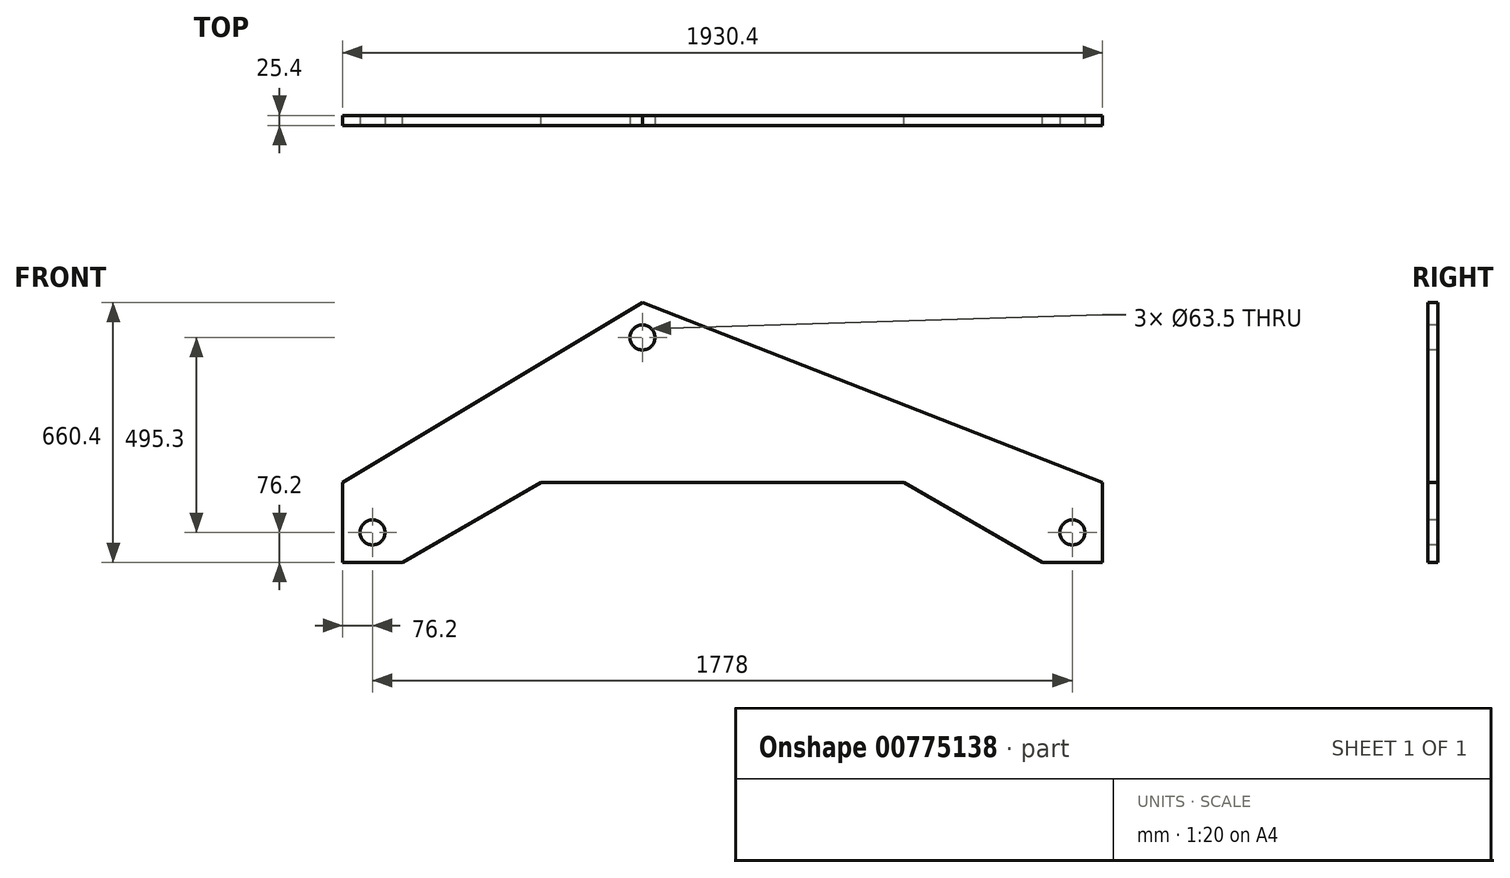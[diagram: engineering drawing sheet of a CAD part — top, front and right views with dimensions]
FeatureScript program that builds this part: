
annotation { "Feature Type Name" : "Feature", "Feature Type Description" : "" }
export const myFeature = defineFeature(function(context is Context, id is Id, definition is map)
    precondition{}
    {
        {
            var Q0;
            Q0=qCreatedBy(makeId("Front.planeOp"),FACE);
            var sketch = newSketch(context, id + "F0", { "sketchPlane" : qUnion([Q0])});
            skLineSegment(sketch, "E0", {"start": v(-762, 0) * mm, "end": v(0, 457.2) * mm});
            skLineSegment(sketch, "E1", {"start": v(0, 457.2) * mm, "end": v(1168.4, 0) * mm});
            skLineSegment(sketch, "E2", {"start": v(1168.4, 0) * mm, "end": v(1168.4, -203.2) * mm});
            skLineSegment(sketch, "E3", {"start": v(1168.4, -203.2) * mm, "end": v(1016, -203.2) * mm});
            skLineSegment(sketch, "E4", {"start": v(1016, -203.2) * mm, "end": v(664.05, 0) * mm});
            skLineSegment(sketch, "E5", {"start": v(664.05, 0) * mm, "end": v(-257.65, 0) * mm});
            skLineSegment(sketch, "E6", {"start": v(-257.65, 0) * mm, "end": v(-609.6, -203.2) * mm});
            skLineSegment(sketch, "E7", {"start": v(-609.6, -203.2) * mm, "end": v(-762, -203.2) * mm});
            skLineSegment(sketch, "E8", {"start": v(-762, -203.2) * mm, "end": v(-762, 0) * mm});
            skSolve(sketch);
        }
        {
            var Q0;
            Q0 = qSketchRegion(id + "F0", true);
            extrude(context, id + "F1", {"entities" : qUnion([Q0]), "depth" : 25.4 * mm, "offsetDistance" : 25.4 * mm});
        }
        {
            var Q0;
            Q0=makeQuery(id+"F1.opExtrude","CAP_FACE",FACE,{"disambiguationData":[OSD([sQuery(id+"F0.wireOp",EDGE,"E0"),sQuery(id+"F0.wireOp",EDGE,"E1"),sQuery(id+"F0.wireOp",EDGE,"E2"),sQuery(id+"F0.wireOp",EDGE,"E3"),sQuery(id+"F0.wireOp",EDGE,"E4"),sQuery(id+"F0.wireOp",EDGE,"E5"),sQuery(id+"F0.wireOp",EDGE,"E6"),sQuery(id+"F0.wireOp",EDGE,"E7"),sQuery(id+"F0.wireOp",EDGE,"E8")])],"isStart":false});
            var sketch = newSketch(context, id + "F2", { "sketchPlane" : qUnion([Q0])});
            skCircle(sketch, "E9", {"center": v(0, 368.3) * mm, "radius": 31.75 * mm});
            skCircle(sketch, "E10", {"center": v(-685.8, -127) * mm, "radius": 31.75 * mm});
            skCircle(sketch, "E11", {"center": v(1092.2, -127) * mm, "radius": 31.75 * mm});
            skSolve(sketch);
        }
        {
            var Q0;
            Q0 = qSketchRegion(id + "F2", true);
            extrude(context, id + "F3", {"entities" : qUnion([Q0]), "operationType" : NewBodyOperationType.REMOVE, "oppositeDirection" : true, "depth" : 50.8 * mm, "offsetDistance" : 25.4 * mm});
        }
    });
